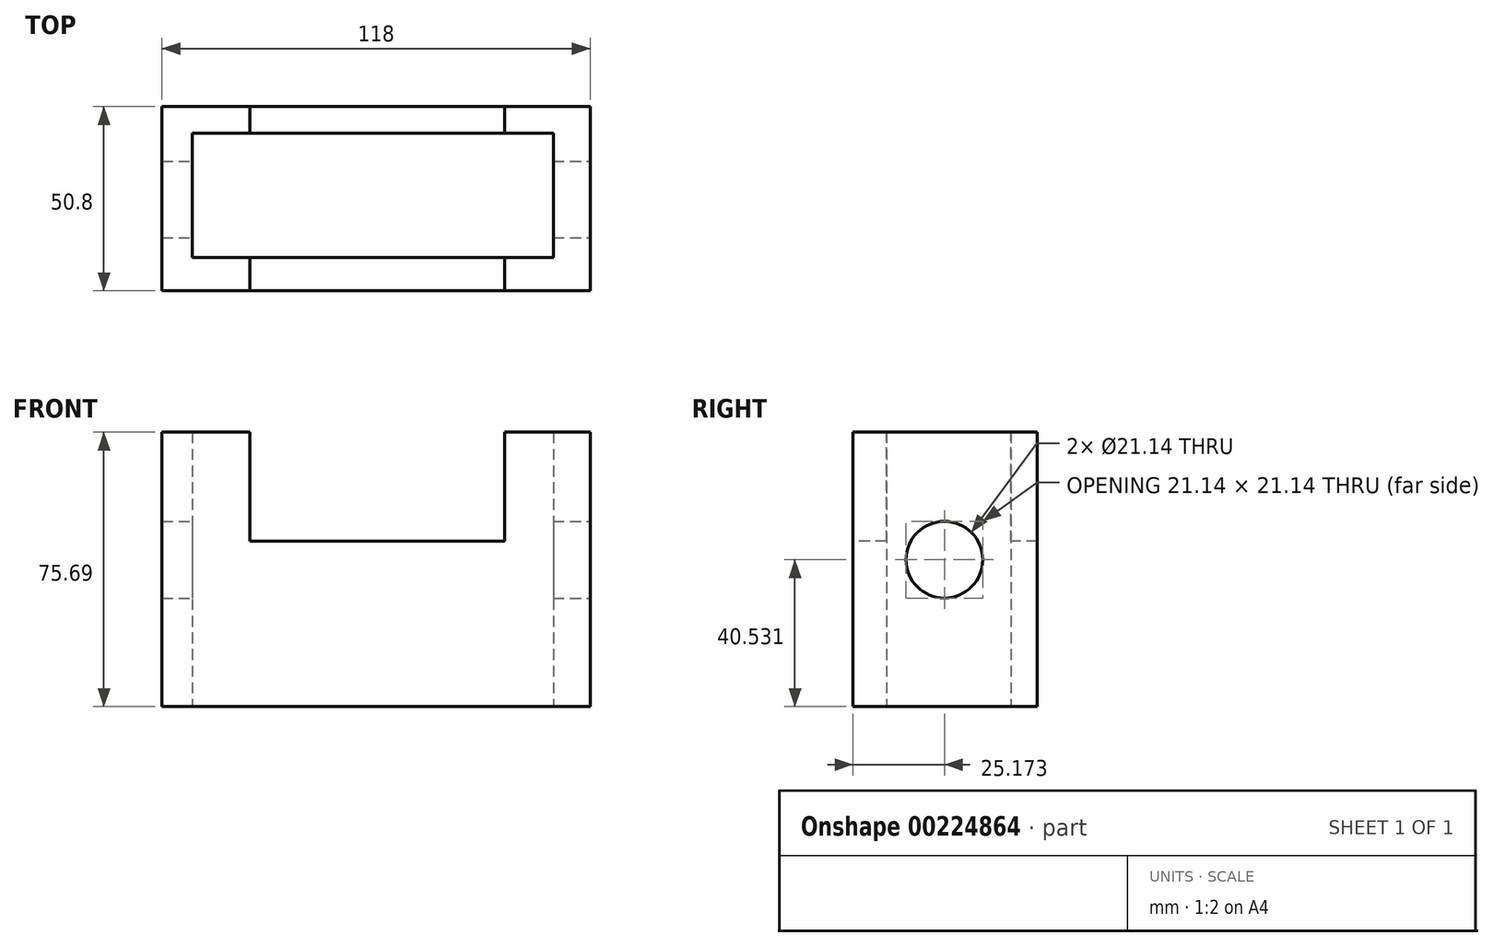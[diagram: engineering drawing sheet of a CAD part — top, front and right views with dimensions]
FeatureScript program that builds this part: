
annotation { "Feature Type Name" : "Feature", "Feature Type Description" : "" }
export const myFeature = defineFeature(function(context is Context, id is Id, definition is map)
    precondition{}
    {
        {
            var Q0;
            Q0=qCreatedBy(makeId("Front.planeOp"),FACE);
            var sketch = newSketch(context, id + "F0", { "sketchPlane" : qUnion([Q0])});
            skLineSegment(sketch, "E0.bottom", {"start": v(-54.83, 40.97) * mm, "end": v(63.17, 40.97) * mm});
            skLineSegment(sketch, "E0.top", {"start": v(-54.83, -34.72) * mm, "end": v(63.17, -34.72) * mm});
            skLineSegment(sketch, "E0.left", {"start": v(-54.83, 40.97) * mm, "end": v(-54.83, -34.72) * mm});
            skLineSegment(sketch, "E0.right", {"start": v(63.17, 40.97) * mm, "end": v(63.17, -34.72) * mm});
            skSolve(sketch);
        }
        {
            var Q0;
            Q0=makeQuery(id+"F0.imprint","IMPRINT",FACE,{"disambiguationData":[TD([[makeQuery(id+"F0.imprint","IMPRINT",EDGE,{"derivedFrom":sQuery(id+"F0.wireOp",EDGE,"E0.bottom")}),-1.0]])]});
            extrude(context, id + "F1", {"entities" : qUnion([Q0]), "depth" : 50.8 * mm});
        }
        {
            var Q0;
            Q0=makeQuery(id+"F1.opExtrude","SWEPT_FACE",FACE,{"disambiguationData":[OSD([sQuery(id+"F0.wireOp",EDGE,"E0.top")])]});
            var sketch = newSketch(context, id + "F2", { "sketchPlane" : qUnion([Q0])});
            skLineSegment(sketch, "E1.bottom", {"start": v(-46.49, 41.57) * mm, "end": v(53.04, 41.57) * mm});
            skLineSegment(sketch, "E1.top", {"start": v(-46.49, 7.3) * mm, "end": v(53.04, 7.3) * mm});
            skLineSegment(sketch, "E1.left", {"start": v(-46.49, 41.57) * mm, "end": v(-46.49, 7.3) * mm});
            skLineSegment(sketch, "E1.right", {"start": v(53.04, 41.57) * mm, "end": v(53.04, 7.3) * mm});
            skSolve(sketch);
        }
        {
            var Q0;
            Q0=makeQuery(id+"F2.imprint","IMPRINT",FACE,{"disambiguationData":[TD([[makeQuery(id+"F2.imprint","IMPRINT",EDGE,{"derivedFrom":sQuery(id+"F2.wireOp",EDGE,"E1.bottom")}),-1.0]])]});
            extrude(context, id + "F3", {"entities" : qUnion([Q0]), "operationType" : NewBodyOperationType.REMOVE, "endBound" : BoundingType.THROUGH_ALL, "oppositeDirection" : true, "depth" : 25.4 * mm});
        }
        {
            var Q0;
            Q0=makeQuery(id+"F1.opExtrude","CAP_FACE",FACE,{"disambiguationData":[OSD([sQuery(id+"F0.wireOp",EDGE,"E0.bottom"),sQuery(id+"F0.wireOp",EDGE,"E0.top"),sQuery(id+"F0.wireOp",EDGE,"E0.left"),sQuery(id+"F0.wireOp",EDGE,"E0.right")])],"isStart":false});
            var sketch = newSketch(context, id + "F4", { "sketchPlane" : qUnion([Q0])});
            skLineSegment(sketch, "E2.bottom", {"start": v(-30.7, 48.72) * mm, "end": v(39.63, 48.72) * mm});
            skLineSegment(sketch, "E2.top", {"start": v(-30.7, 10.88) * mm, "end": v(39.63, 10.88) * mm});
            skLineSegment(sketch, "E2.left", {"start": v(-30.7, 48.72) * mm, "end": v(-30.7, 10.88) * mm});
            skLineSegment(sketch, "E2.right", {"start": v(39.63, 48.72) * mm, "end": v(39.63, 10.88) * mm});
            skSolve(sketch);
        }
        {
            var Q0;
            {var subQ0=sQuery(id+"F4.wireOp",EDGE,"E2.top");Q0=makeQuery(id+"F4.imprint","IMPRINT",FACE,{"disambiguationData":[TD([[makeQuery(id+"F4.imprint","IMPRINT",EDGE,{"derivedFrom":subQ0}),1.0]])]});}
            var Q1;
            {var subQ0=sQuery(id+"F4.wireOp",EDGE,"E2.bottom");Q1=makeQuery(id+"F4.imprint","IMPRINT",FACE,{"disambiguationData":[TD([[makeQuery(id+"F4.imprint","IMPRINT",EDGE,{"derivedFrom":subQ0}),-1.0]])]});}
            extrude(context, id + "F5", {"entities" : qUnion([Q0, Q1]), "operationType" : NewBodyOperationType.REMOVE, "endBound" : BoundingType.THROUGH_ALL, "oppositeDirection" : true, "depth" : 25.4 * mm});
        }
        {
            var Q0;
            Q0=makeQuery(id+"F1.opExtrude","SWEPT_FACE",FACE,{"disambiguationData":[OSD([sQuery(id+"F0.wireOp",EDGE,"E0.right")])]});
            var sketch = newSketch(context, id + "F6", { "sketchPlane" : qUnion([Q0])});
            skCircle(sketch, "E3", {"center": v(-25.63, 5.81) * mm, "radius": 10.57 * mm});
            skSolve(sketch);
        }
        {
            var Q0;
            Q0=makeQuery(id+"F6.imprint","IMPRINT",FACE,{"disambiguationData":[TD([[makeQuery(id+"F6.imprint","IMPRINT",EDGE,{"derivedFrom":sQuery(id+"F6.wireOp",EDGE,"E3")}),1.0]])]});
            extrude(context, id + "F7", {"entities" : qUnion([Q0]), "operationType" : NewBodyOperationType.REMOVE, "endBound" : BoundingType.THROUGH_ALL, "oppositeDirection" : true, "depth" : 25.4 * mm});
        }
    });
